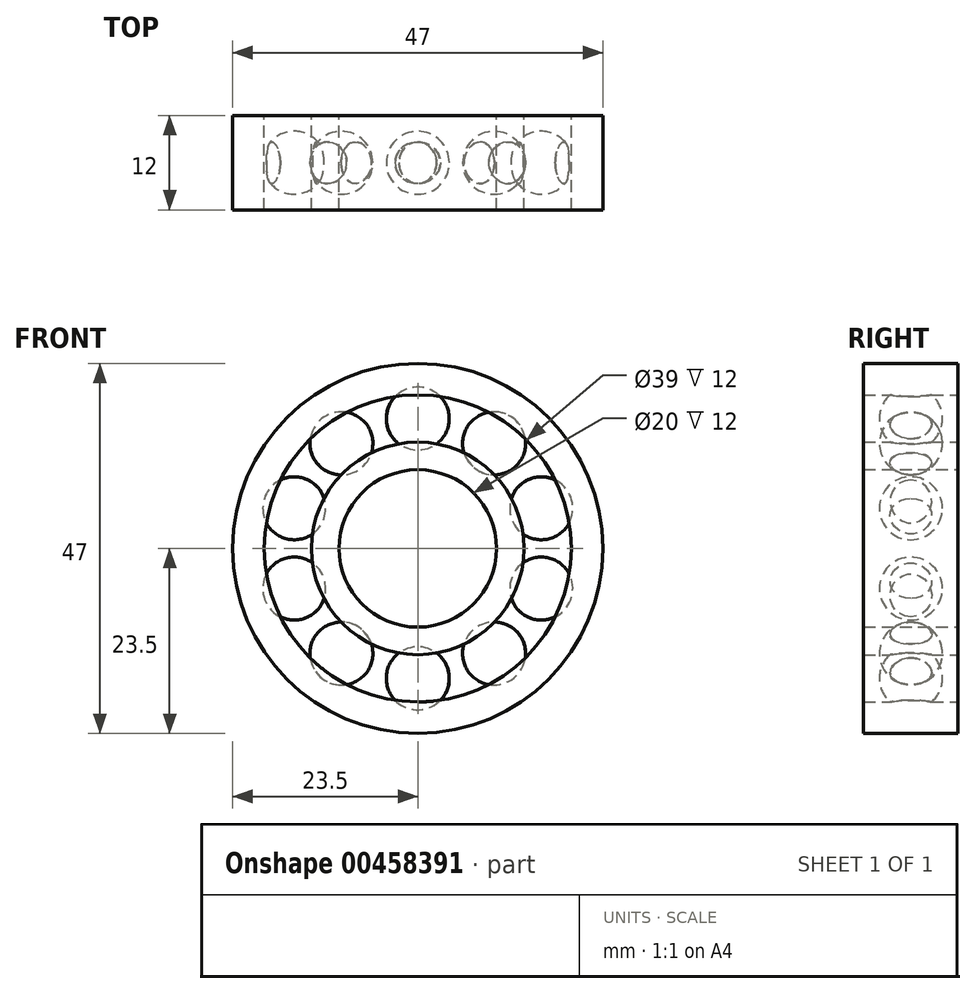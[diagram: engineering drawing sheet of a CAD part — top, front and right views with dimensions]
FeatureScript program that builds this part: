
annotation { "Feature Type Name" : "Feature", "Feature Type Description" : "" }
export const myFeature = defineFeature(function(context is Context, id is Id, definition is map)
    precondition{}
    {
        {
            var Q0;
            Q0=qCreatedBy(makeId("Front.planeOp"),FACE);
            var sketch = newSketch(context, id + "F0", { "sketchPlane" : qUnion([Q0])});
            skCircle(sketch, "E0", {"center": v(0, 0) * mm, "radius": 19.5 * mm});
            skCircle(sketch, "E1", {"center": v(0, 0) * mm, "radius": 23.5 * mm});
            skCircle(sketch, "E2", {"center": v(0, 0) * mm, "radius": 10 * mm});
            skCircle(sketch, "E3", {"center": v(0, 0) * mm, "radius": 13.5 * mm});
            skSolve(sketch);
        }
        {
            var Q0;
            Q0 = qSketchRegion(id + "F0", true);
            var Q1;
            Q1=makeQuery(id+"F0.imprint","IMPRINT",FACE,{"disambiguationData":[TD([[makeQuery(id+"F0.imprint","IMPRINT",EDGE,{"derivedFrom":sQuery(id+"F0.wireOp",EDGE,"E0")}),-1.0]])]});
            var Q2;
            Q2=makeQuery(id+"F0.imprint","IMPRINT",FACE,{"disambiguationData":[TD([[makeQuery(id+"F0.imprint","IMPRINT",EDGE,{"derivedFrom":sQuery(id+"F0.wireOp",EDGE,"E2")}),-1.0]])]});
            extrude(context, id + "F1", {"entities" : qUnion([Q0, Q1, Q2]), "depth" : 12 * mm});
        }
        {
            var Q0;
            Q0=qCreatedBy(makeId("Front.planeOp"),FACE);
            cPlane(context, id + "F2", {"entities" : qUnion([Q0]), "cplaneType" : CPlaneType.OFFSET, "offset" : 6 * mm, "width" : 150 * mm, "height" : 150 * mm});
        }
        {
            var Q0;
            Q0=qCreatedBy(id+"F2.planeOp",FACE);
            var sketch = newSketch(context, id + "F3", { "sketchPlane" : qUnion([Q0])});
            skArc(sketch, "E4", {"start": v(0, 12.5) * mm, "mid": v(4, 16.5) * mm, "end": v(0, 20.5) * mm});
            skLineSegment(sketch, "E5", {"start": v(0, 20.5) * mm, "end": v(0, 12.5) * mm});
            skSolve(sketch);
        }
        {
            var Q0;
            Q0 = qSketchRegion(id + "F3", true);
            var Q1;
            Q1=sQuery(id+"F3.wireOp",EDGE,"E5");
            revolve(context, id + "F4", {"entities" : qUnion([Q0]), "axis" : qUnion([Q1]), "revolveType" : RevolveType.FULL});
        }
        {
            var Q0;
            Q0=qCreatedBy(makeId("Top.planeOp"),FACE);
            var sketch = newSketch(context, id + "F5", { "sketchPlane" : qUnion([Q0])});
            skLineSegment(sketch, "E6", {"start": v(0, 0) * mm, "end": v(0, -77.4) * mm, "construction": true});
            skSolve(sketch);
        }
        {
            var Q0;
            Q0=makeQuery(id+"F4.opRevolve","SWEPT_BODY",BODY,{"disambiguationData":[OSD([sQuery(id+"F3.wireOp",EDGE,"E4"),sQuery(id+"F3.wireOp",EDGE,"E5")])]});
            var Q1;
            Q1=sQuery(id+"F5.wireOp",EDGE,"E6");
            circularPattern(context, id + "F6", {"operationType" : NewBodyOperationType.ADD, "entities" : qUnion([Q0]), "axis" : qUnion([Q1]), "angle" : 360 * degree, "instanceCount" : 10, "equalSpace" : true});
        }
    });
